# Revit family: CCD-103_Central de detección y extinción
name_source: partatom
category: Equipos eléctricos
revit_build: Autodesk Revit 2017 (Build: 20190508_0315(x64)
units: mm (PartAtom-declared; Revit-internal decimal feet)

## family parameters
Anfitrión = Cara
Compartido = No
Corte con vacíos al cargar = No
Cota de conector redondo = Diámetro de uso
Punto de cálculo de habitación = No
Tipo de pieza = Otro panel

## types (1)
- CCD-103
    Altura = 443 mm
    Anchura = 268 mm
    Baterías = 2 x 7.5 Ah
    Carga eléctrica = Otro
    Carga máxima de sirenas (por salida) = 450 mA
    Certificación = EN 54-2, EN 54-4 y EN 12094-1
    Comentarios de tipo = La central detección CCD-103 combina la funcionalidad de una central convencional de detección con el añadido de las prestaciones necesarias para hacer funcionar el sistema de extinción de incendios, cuyo propósito es extinguir el fuego de la manera más eficaz posible. El método de accionamiento desde la central puede ser automático a través de los detectores que se conectan a las zonas de detección o manualmente a través de los pulsadores de disparo.
    Corriente máxima bloque extinción = 450 mA
    Corriente máxima en alarma de las zonas = 82 mA
    Corriente máxima en reposo para detectores = 4 mA
    Código de montaje = PDETCCD-103
    Descripción = La central convencional de extinción de Detnov CCD-103 es una solución compacta para un sistema de detección y
extinción. Ha sido certificada según las normas EN 12094-1, EN 54-2 y EN 54-4. La CCD-103 está compuesta por dos
bloques, un bloque de detección y un bloque de extinción.
    Elevación por defecto = 1219 mm
    Fabricante = Detnov Security
    Fases = 1
    Humedad relativa = 95% sin condensación
    Imagen de tipo = <Ninguno>
    Modelo = Central CCD-103
    Número máximo de dispositivos por zona = 32 detectores / 10 pulsadores
    Peso (sin baterías) = 1.90 kg
    Potencia máxima de conmutación = 10A a 30VCC
    Potencia total = 0 VA
    Profundidad = 109 mm
    Relé ventilación libre de tensión = 1 relé con contactos C, NA, NC
    Resistencia máxima de la línea de zona = 44.0000 ohm·m
    Retardo seleccionable en placa = 0 - 10 minutos
    Salida 24V auxiliar = 450 mA
    Salidas relés libres de tensión = 10A a 30VCC
    Teléfono = (+34) 93 371 60 25
    Temperatura trabajo = De -5ºC a 50ºC
    Tensión de alimentación = 90-264V / AC / 50/60 Hz
    Tensión de salida activada en sirenas, botella y estados de extinción = Min. 18VCC Max. 29VCC
    Tensión de salida en reposo en sirenas, botella y estados de extinción = De -5VCC a -9VCC
    URL = https://www.detnov.com
    Voltaje_x = 230 V
    Índice IP = IP30
